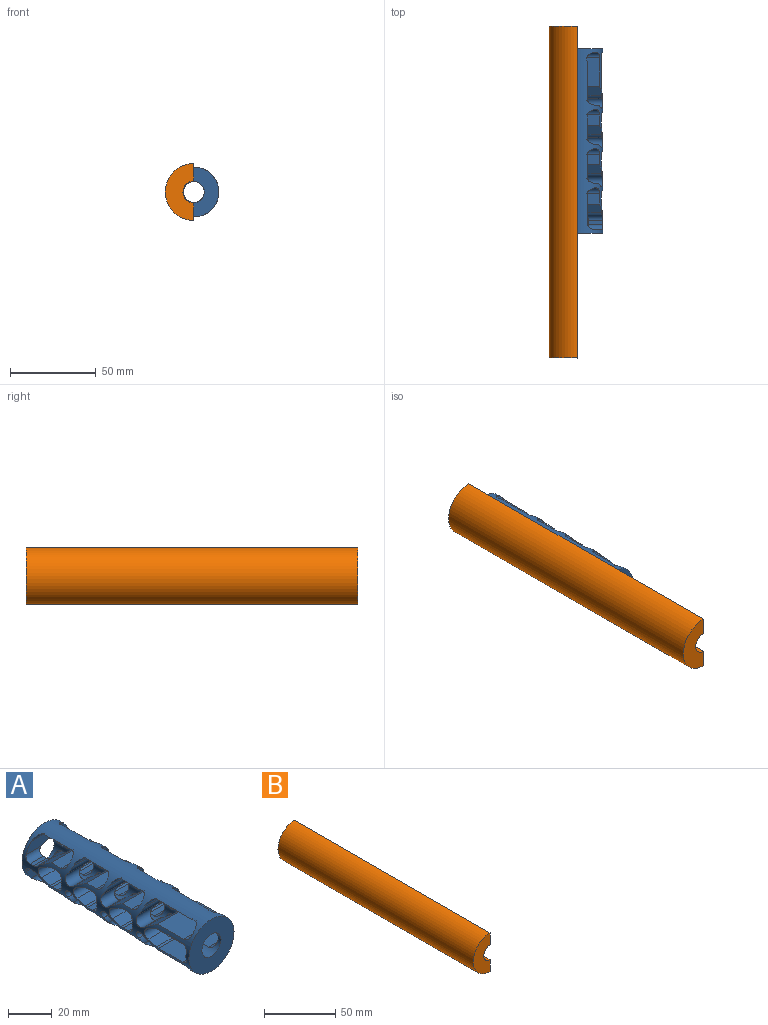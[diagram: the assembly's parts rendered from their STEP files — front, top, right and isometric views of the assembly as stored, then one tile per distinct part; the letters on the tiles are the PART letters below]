
ASSEMBLY  parts=2 mates=1
PART A: 185 faces, bbox 29.1x107.6x29.1 mm
  f0: plane 8.74x4.19mm, normal (0,1,0), area 35.3mm2, adj f57,f61,f183,f184
  f1: plane 15.44x10.34mm, normal (0,0,1), area 159.6mm2, adj f3,f57,f61,f184
  f2: plane 15.44x10.34mm, normal (0,0,1), area 159.6mm2, adj f61,f65,f180,f184
  f3: cylinder r=3.17mm len=10.43mm, axis (1,0,0), area 12.9mm2, adj f1,f4,f61,f184
  f4: plane 10.65x4.96mm, normal (0,-0.39,0.92), area 50.1mm2, adj f3,f5,f61,f184
  f5: cylinder r=3.2mm len=9.12mm, axis (1,0,0), area 63.7mm2, adj f4,f6,f61,f184
  f6: plane 10.67x4.96mm, normal (0,-0.39,-0.92), area 50.2mm2, adj f5,f7,f61,f184
  f7: cylinder r=3.17mm len=10.46mm, axis (1,0,0), area 13mm2, adj f6,f8,f61,f184
  f8: plane 15.39x10.36mm, normal (0,0,-1), area 159.5mm2, adj f7,f61,f183,f184
  f9: plane 15.39x10.36mm, normal (0,0,-1), area 159.5mm2, adj f58,f61,f69,f184
  f10: cylinder r=4.43mm len=9.66mm, axis (1,0,0), area 20.6mm2, adj f61,f73,f75,f184
  f11: plane 25.34x16.92mm, normal (0,0,-1), area 428.7mm2, adj f61,f75,f181
  f12: plane 25.34x16.92mm, normal (0,0,1), area 428.7mm2, adj f61,f80,f182
  f13: cylinder r=4.43mm len=9.66mm, axis (1,0,0), area 20.5mm2, adj f61,f80,f82,f184
  f14: plane 10.34x3.44mm, normal (0,0,1), area 35.5mm2, adj f15,f23,f61,f184
  f15: cylinder r=3.17mm len=10.43mm, axis (1,0,0), area 12.9mm2, adj f14,f16,f61,f184
  f16: plane 10.65x4.96mm, normal (0,-0.39,0.92), area 50.1mm2, adj f15,f17,f61,f184
  f17: cylinder r=3.2mm len=9.12mm, axis (1,0,0), area 63.7mm2, adj f16,f18,f61,f184
  f18: plane 10.67x4.96mm, normal (0,-0.39,-0.92), area 50.2mm2, adj f17,f19,f61,f184
  f19: cylinder r=3.17mm len=10.46mm, axis (1,0,0), area 13mm2, adj f18,f20,f61,f184
  f20: plane 10.36x3.38mm, normal (0,0,-1), area 35mm2, adj f19,f21,f61,f184
  f21: cylinder r=3.17mm len=11.05mm, axis (1,0,0), area 39.6mm2, adj f20,f22,f61,f184
  f22: cylinder r=10.73mm len=9.15mm, axis (1,0,0), area 51.3mm2, adj f21,f23,f61,f184
  f23: cylinder r=3.17mm len=11.02mm, axis (1,0,0), area 39.6mm2, adj f14,f22,f61,f184
  f24: cylinder r=4.43mm len=9.66mm, axis (1,0,0), area 20.6mm2, adj f61,f98,f100,f184
  f25: cylinder r=4.43mm len=9.66mm, axis (1,0,0), area 20.5mm2, adj f61,f109,f111,f184
  f26: plane 10.34x3.44mm, normal (0,0,1), area 35.5mm2, adj f27,f35,f61,f184
  f27: cylinder r=3.17mm len=10.43mm, axis (1,0,0), area 12.9mm2, adj f26,f28,f61,f184
  f28: plane 10.65x4.96mm, normal (0,-0.39,0.92), area 50.1mm2, adj f27,f29,f61,f184
  f29: cylinder r=3.2mm len=9.12mm, axis (1,0,0), area 63.7mm2, adj f28,f30,f61,f184
  f30: plane 10.67x4.96mm, normal (0,-0.39,-0.92), area 50.2mm2, adj f29,f31,f61,f184
  f31: cylinder r=3.17mm len=10.46mm, axis (1,0,0), area 13mm2, adj f30,f32,f61,f184
  f32: plane 10.36x3.38mm, normal (0,0,-1), area 35mm2, adj f31,f33,f61,f184
  f33: cylinder r=3.17mm len=11.05mm, axis (1,0,0), area 39.6mm2, adj f32,f34,f61,f184
  f34: cylinder r=10.73mm len=9.15mm, axis (1,0,0), area 51.3mm2, adj f33,f35,f61,f184
  f35: cylinder r=3.17mm len=11.02mm, axis (1,0,0), area 39.6mm2, adj f26,f34,f61,f184
  f36: cylinder r=4.43mm len=9.66mm, axis (1,0,0), area 20.6mm2, adj f61,f127,f129,f184
  f37: cylinder r=4.43mm len=9.66mm, axis (1,0,0), area 20.5mm2, adj f61,f138,f140,f184
  f38: plane 10.34x3.44mm, normal (0,0,1), area 35.5mm2, adj f39,f47,f61,f184
  f39: cylinder r=3.17mm len=10.43mm, axis (1,0,0), area 12.9mm2, adj f38,f40,f61,f184
  f40: plane 10.65x4.96mm, normal (0,-0.39,0.92), area 50.1mm2, adj f39,f41,f61,f184
  f41: cylinder r=3.2mm len=9.12mm, axis (1,0,0), area 63.7mm2, adj f40,f42,f61,f184
  f42: plane 10.67x4.96mm, normal (0,-0.39,-0.92), area 50.2mm2, adj f41,f43,f61,f184
  f43: cylinder r=3.17mm len=10.46mm, axis (1,0,0), area 13mm2, adj f42,f44,f61,f184
  f44: plane 10.36x3.38mm, normal (0,0,-1), area 35mm2, adj f43,f45,f61,f184
  f45: cylinder r=3.17mm len=11.05mm, axis (1,0,0), area 39.6mm2, adj f44,f46,f61,f184
  f46: cylinder r=10.73mm len=9.15mm, axis (1,0,0), area 51.3mm2, adj f45,f47,f61,f184
  f47: cylinder r=3.17mm len=11.02mm, axis (1,0,0), area 39.6mm2, adj f38,f46,f61,f184
  f48: cylinder r=3.17mm len=8.92mm, axis (1,0,0), area 24.6mm2, adj f49,f56,f61,f184
  f49: cylinder r=4.43mm len=9.66mm, axis (1,0,0), area 20.6mm2, adj f48,f61,f155,f184
  f50: cylinder r=4.43mm len=9.66mm, axis (1,0,0), area 20.5mm2, adj f51,f61,f162,f184
  f51: cylinder r=3.17mm len=8.92mm, axis (1,0,0), area 24.6mm2, adj f50,f53,f61,f184
  f52: cylinder r=3.17mm len=10.43mm, axis (1,0,0), area 43.9mm2, adj f53,f61,f172,f184
  f53: plane 8.48x2.48mm, normal (0,0,1), area 21.1mm2, adj f51,f52,f61,f184
  f54: cylinder r=3.17mm len=10.4mm, axis (1,0,0), area 43.9mm2, adj f55,f61,f176,f184
  f55: plane 8.47x2.48mm, normal (0,0,-1), area 21mm2, adj f54,f56,f61,f184
  f56: plane 8.48x0.03mm, normal (0,1,0), area 0.2mm2, adj f48,f55,f61,f184
  f57: cylinder r=3.17mm len=11.17mm, axis (1,0,0), area 47.3mm2, adj f0,f1,f61,f184
  f58: cylinder r=3.17mm len=11.2mm, axis (-1,0,0), area 47.4mm2, adj f9,f60,f61,f184
  f59: plane 20.52x0.06mm, normal (0,1,0), area 1.1mm2, adj f61,f165,f181
  f60: plane 8.74x4.19mm, normal (0,1,0), area 35.3mm2, adj f58,f61,f180,f184
  f61: cylinder r=14.53mm len=107.57mm, axis (0,1,0), area 4158.4mm2, adj f0,f1,f2,f3,f4,f5,f6,f7
  f62: cylinder r=3.18mm len=10.94mm, axis (1,0,0), area 6.7mm2, adj f61,f76,f166
  f63: plane 29.06x29.06mm, normal (0,-1,0), area 544mm2, adj f61,f184
  f64: plane 29.06x29.06mm, normal (0,1,0), area 544mm2, adj f61,f184
  f65: cylinder r=3.17mm len=10.43mm, axis (1,0,0), area 12.9mm2, adj f2,f61,f66,f184
  f66: plane 10.65x4.96mm, normal (0,-0.39,0.92), area 50.1mm2, adj f61,f65,f67,f184
  f67: cylinder r=3.2mm len=9.12mm, axis (1,0,0), area 63.7mm2, adj f61,f66,f68,f184
  f68: plane 10.67x4.96mm, normal (0,-0.39,-0.92), area 50.2mm2, adj f61,f67,f69,f184
  f69: cylinder r=3.17mm len=10.46mm, axis (1,0,0), area 13mm2, adj f9,f61,f68,f184
  f70: cylinder r=3.17mm len=20.9mm, axis (1,0,0), area 73.1mm2, adj f61,f71,f76
  f71: cylinder r=5.04mm len=25.84mm, axis (1,0,0), area 87.1mm2, adj f61,f70,f72
  f72: cylinder r=10.78mm len=25.88mm, axis (1,0,0), area 1.4mm2, adj f61,f71,f73
  f73: cylinder r=3.17mm len=28.91mm, axis (1,0,0), area 184.8mm2, adj f10,f61,f72,f74,f184
  f74: cylinder r=4.43mm len=9.66mm, axis (1,0,0), area 20.6mm2, adj f61,f73,f75,f184
  f75: plane 27.89x5.13mm, normal (0,0.51,-0.86), area 133.2mm2, adj f10,f11,f61,f74,f184
  f76: plane 22.91x10.94mm, normal (0,0,1), area 250.5mm2, adj f61,f62,f70
  f77: cylinder r=5.04mm len=25.83mm, axis (1,0,0), area 87mm2, adj f61,f78,f84
  f78: cylinder r=3.17mm len=20.9mm, axis (1,0,0), area 73.1mm2, adj f61,f77,f79
  f79: plane 22.88x10.94mm, normal (0,0,-1), area 250.3mm2, adj f61,f78,f167
  f80: plane 27.89x5.13mm, normal (0,0.51,0.86), area 133.3mm2, adj f12,f13,f61,f81,f184
  f81: cylinder r=4.43mm len=9.66mm, axis (1,0,0), area 20.5mm2, adj f61,f80,f82,f184
  f82: cylinder r=3.17mm len=28.91mm, axis (1,0,0), area 184.8mm2, adj f13,f61,f81,f83,f184
  f83: cylinder r=10.78mm len=25.88mm, axis (1,0,0), area 1.4mm2, adj f61,f82,f84
  f84: plane 25.84x0mm, normal (0,-0.79,-0.62), area 0.1mm2, adj f61,f77,f83
  f85: plane 10.34x3.44mm, normal (0,0,1), area 35.5mm2, adj f61,f86,f94,f184
  f86: cylinder r=3.17mm len=10.43mm, axis (1,0,0), area 12.9mm2, adj f61,f85,f87,f184
  f87: plane 10.65x4.96mm, normal (0,-0.39,0.92), area 50.1mm2, adj f61,f86,f88,f184
  f88: cylinder r=3.2mm len=9.12mm, axis (1,0,0), area 63.7mm2, adj f61,f87,f89,f184
  f89: plane 10.67x4.96mm, normal (0,-0.39,-0.92), area 50.2mm2, adj f61,f88,f90,f184
  f90: cylinder r=3.17mm len=10.46mm, axis (1,0,0), area 13mm2, adj f61,f89,f91,f184
  f91: plane 10.36x3.38mm, normal (0,0,-1), area 35mm2, adj f61,f90,f92,f184
  f92: cylinder r=3.17mm len=11.05mm, axis (1,0,0), area 39.6mm2, adj f61,f91,f93,f184
  f93: cylinder r=10.73mm len=9.15mm, axis (1,0,0), area 51.3mm2, adj f61,f92,f94,f184
  f94: cylinder r=3.17mm len=11.02mm, axis (1,0,0), area 39.6mm2, adj f61,f85,f93,f184
  f95: cylinder r=3.17mm len=20.9mm, axis (1,0,0), area 73.1mm2, adj f61,f96,f103
  f96: cylinder r=5.04mm len=25.84mm, axis (1,0,0), area 87.1mm2, adj f61,f95,f97
  f97: cylinder r=10.78mm len=25.88mm, axis (1,0,0), area 1.4mm2, adj f61,f96,f98
  f98: cylinder r=3.17mm len=28.91mm, axis (1,0,0), area 184.8mm2, adj f24,f61,f97,f99,f184
  f99: cylinder r=4.43mm len=9.66mm, axis (1,0,0), area 20.6mm2, adj f61,f98,f100,f184
  f100: plane 27.89x5.13mm, normal (0,0.51,-0.86), area 133.2mm2, adj f24,f61,f99,f101,f184
  f101: plane 25.34x6.28mm, normal (0,0,-1), area 159.2mm2, adj f61,f100,f102
  f102: cylinder r=3.18mm len=25.34mm, axis (1,0,0), area 193.1mm2, adj f61,f101,f103
  f103: plane 14.54x10.94mm, normal (0,0,1), area 159mm2, adj f61,f95,f102
  f104: cylinder r=5.04mm len=25.83mm, axis (1,0,0), area 87mm2, adj f61,f105,f113
  f105: cylinder r=3.17mm len=20.9mm, axis (1,0,0), area 73.1mm2, adj f61,f104,f106
  f106: plane 14.54x10.94mm, normal (0,0,-1), area 159mm2, adj f61,f105,f107
  f107: cylinder r=3.17mm len=25.34mm, axis (1,0,0), area 193.4mm2, adj f61,f106,f108
  f108: plane 25.34x6.28mm, normal (0,0,1), area 159.2mm2, adj f61,f107,f109
  f109: plane 27.89x5.13mm, normal (0,0.51,0.86), area 133.3mm2, adj f25,f61,f108,f110,f184
  f110: cylinder r=4.43mm len=9.66mm, axis (1,0,0), area 20.5mm2, adj f61,f109,f111,f184
  f111: cylinder r=3.17mm len=28.91mm, axis (1,0,0), area 184.8mm2, adj f25,f61,f110,f112,f184
  f112: cylinder r=10.78mm len=25.88mm, axis (1,0,0), area 1.4mm2, adj f61,f111,f113
  f113: plane 25.84x0mm, normal (0,-0.79,-0.62), area 0.1mm2, adj f61,f104,f112
  f114: plane 10.34x3.44mm, normal (0,0,1), area 35.5mm2, adj f61,f115,f123,f184
  f115: cylinder r=3.17mm len=10.43mm, axis (1,0,0), area 12.9mm2, adj f61,f114,f116,f184
  f116: plane 10.65x4.96mm, normal (0,-0.39,0.92), area 50.1mm2, adj f61,f115,f117,f184
  f117: cylinder r=3.2mm len=9.12mm, axis (1,0,0), area 63.7mm2, adj f61,f116,f118,f184
  f118: plane 10.67x4.96mm, normal (0,-0.39,-0.92), area 50.2mm2, adj f61,f117,f119,f184
  f119: cylinder r=3.17mm len=10.46mm, axis (1,0,0), area 13mm2, adj f61,f118,f120,f184
  f120: plane 10.36x3.38mm, normal (0,0,-1), area 35mm2, adj f61,f119,f121,f184
  f121: cylinder r=3.17mm len=11.05mm, axis (1,0,0), area 39.6mm2, adj f61,f120,f122,f184
  f122: cylinder r=10.73mm len=9.15mm, axis (1,0,0), area 51.3mm2, adj f61,f121,f123,f184
  f123: cylinder r=3.17mm len=11.02mm, axis (1,0,0), area 39.6mm2, adj f61,f114,f122,f184
  f124: cylinder r=3.17mm len=20.9mm, axis (1,0,0), area 73.1mm2, adj f61,f125,f132
  f125: cylinder r=5.04mm len=25.84mm, axis (1,0,0), area 87.1mm2, adj f61,f124,f126
  f126: cylinder r=10.78mm len=25.88mm, axis (1,0,0), area 1.4mm2, adj f61,f125,f127
  f127: cylinder r=3.17mm len=28.91mm, axis (1,0,0), area 184.8mm2, adj f36,f61,f126,f128,f184
  f128: cylinder r=4.43mm len=9.66mm, axis (1,0,0), area 20.6mm2, adj f61,f127,f129,f184
  f129: plane 27.89x5.13mm, normal (0,0.51,-0.86), area 133.2mm2, adj f36,f61,f128,f130,f184
  f130: plane 25.34x6.28mm, normal (0,0,-1), area 159.2mm2, adj f61,f129,f131
  f131: cylinder r=3.18mm len=25.34mm, axis (1,0,0), area 193.1mm2, adj f61,f130,f132
  f132: plane 14.54x10.94mm, normal (0,0,1), area 159mm2, adj f61,f124,f131
  f133: cylinder r=5.04mm len=25.83mm, axis (1,0,0), area 87mm2, adj f61,f134,f142
  f134: cylinder r=3.17mm len=20.9mm, axis (1,0,0), area 73.1mm2, adj f61,f133,f135
  f135: plane 14.54x10.94mm, normal (0,0,-1), area 159mm2, adj f61,f134,f136
  f136: cylinder r=3.17mm len=25.34mm, axis (1,0,0), area 193.4mm2, adj f61,f135,f137
  f137: plane 25.34x6.28mm, normal (0,0,1), area 159.2mm2, adj f61,f136,f138
  f138: plane 27.89x5.13mm, normal (0,0.51,0.86), area 133.3mm2, adj f37,f61,f137,f139,f184
  f139: cylinder r=4.43mm len=9.66mm, axis (1,0,0), area 20.5mm2, adj f61,f138,f140,f184
  f140: cylinder r=3.17mm len=28.91mm, axis (1,0,0), area 184.8mm2, adj f37,f61,f139,f141,f184
  f141: cylinder r=10.78mm len=25.88mm, axis (1,0,0), area 1.4mm2, adj f61,f140,f142
  f142: plane 25.84x0mm, normal (0,-0.79,-0.62), area 0.1mm2, adj f61,f133,f141
  f143: plane 10.34x3.44mm, normal (0,0,1), area 35.5mm2, adj f61,f144,f152,f184
  f144: cylinder r=3.17mm len=10.43mm, axis (1,0,0), area 12.9mm2, adj f61,f143,f145,f184
  f145: plane 10.65x4.96mm, normal (0,-0.39,0.92), area 50.1mm2, adj f61,f144,f146,f184
  f146: cylinder r=3.2mm len=9.12mm, axis (1,0,0), area 63.7mm2, adj f61,f145,f147,f184
  f147: plane 10.67x4.96mm, normal (0,-0.39,-0.92), area 50.2mm2, adj f61,f146,f148,f184
  f148: cylinder r=3.17mm len=10.46mm, axis (1,0,0), area 13mm2, adj f61,f147,f149,f184
  f149: plane 10.36x3.38mm, normal (0,0,-1), area 35mm2, adj f61,f148,f150,f184
  f150: cylinder r=3.17mm len=11.05mm, axis (1,0,0), area 39.6mm2, adj f61,f149,f151,f184
  f151: cylinder r=10.73mm len=9.15mm, axis (1,0,0), area 51.3mm2, adj f61,f150,f152,f184
  f152: cylinder r=3.17mm len=11.02mm, axis (1,0,0), area 39.6mm2, adj f61,f143,f151,f184
  f153: cylinder r=3.17mm len=8.92mm, axis (1,0,0), area 24.6mm2, adj f61,f154,f179,f184
  f154: cylinder r=4.43mm len=9.66mm, axis (1,0,0), area 20.6mm2, adj f61,f153,f155,f184
  f155: plane 27.89x5.13mm, normal (0,0.51,-0.86), area 133.2mm2, adj f49,f61,f154,f156,f184
  f156: plane 25.34x6.28mm, normal (0,0,-1), area 159.2mm2, adj f61,f155,f157
  f157: cylinder r=3.18mm len=25.34mm, axis (1,0,0), area 193.1mm2, adj f61,f156,f158
  f158: plane 18.19x10.94mm, normal (0,0,1), area 199mm2, adj f61,f157,f175
  f159: plane 18.19x10.94mm, normal (0,0,-1), area 199mm2, adj f61,f160,f173
  f160: cylinder r=3.17mm len=25.34mm, axis (1,0,0), area 193.4mm2, adj f61,f159,f161
  f161: plane 25.34x6.28mm, normal (0,0,1), area 159.2mm2, adj f61,f160,f162
  f162: plane 27.89x5.13mm, normal (0,0.51,0.86), area 133.3mm2, adj f50,f61,f161,f163,f184
  f163: cylinder r=4.43mm len=9.66mm, axis (1,0,0), area 20.5mm2, adj f61,f162,f164,f184
  f164: cylinder r=3.17mm len=8.92mm, axis (1,0,0), area 24.6mm2, adj f61,f163,f174,f184
  f165: cylinder r=3.17mm len=20.41mm, axis (1,0,0), area 73.9mm2, adj f59,f61,f166
  f166: plane 10.66x1.65mm, normal (0,0,1), area 17.6mm2, adj f61,f62,f165
  f167: cylinder r=3.18mm len=10.94mm, axis (1,0,0), area 6.7mm2, adj f61,f79,f168
  f168: plane 10.66x1.68mm, normal (0,0,-1), area 17.9mm2, adj f61,f167,f169
  f169: cylinder r=3.17mm len=20.41mm, axis (1,0,0), area 73.9mm2, adj f61,f168,f170
  f170: plane 20.52x0.06mm, normal (0,1,0), area 1.1mm2, adj f61,f169,f182
  f171: cylinder r=3.17mm len=10.43mm, axis (1,0,0), area 43.9mm2, adj f61,f172,f174,f184
  f172: plane 27.52x5.62mm, normal (0,-1,0), area 130.2mm2, adj f52,f61,f171,f173,f184
  f173: cylinder r=3.17mm len=20.52mm, axis (1,0,0), area 74.9mm2, adj f61,f159,f172
  f174: plane 8.48x2.48mm, normal (0,0,1), area 21.1mm2, adj f61,f164,f171,f184
  f175: cylinder r=3.17mm len=20.52mm, axis (1,0,0), area 74.9mm2, adj f61,f158,f176
  f176: plane 27.54x5.65mm, normal (0,-1,0), area 130.7mm2, adj f54,f61,f175,f177,f184
  f177: cylinder r=3.17mm len=10.4mm, axis (1,0,0), area 43.9mm2, adj f61,f176,f178,f184
  f178: plane 8.47x2.48mm, normal (0,0,-1), area 21mm2, adj f61,f177,f179,f184
  f179: plane 8.48x0.03mm, normal (0,1,0), area 0.2mm2, adj f61,f153,f178,f184
  f180: cylinder r=3.17mm len=11.17mm, axis (1,0,0), area 47.3mm2, adj f2,f60,f61,f184
  f181: cylinder r=3.17mm len=25.34mm, axis (1,0,0), area 118.6mm2, adj f11,f59,f61
  f182: cylinder r=3.17mm len=25.34mm, axis (1,0,0), area 118.6mm2, adj f12,f61,f170
  f183: cylinder r=3.17mm len=11.2mm, axis (-1,0,0), area 47.4mm2, adj f0,f8,f61,f184
  f184: cylinder r=6.16mm len=107.57mm, axis (0,-1,0), area 1581.8mm2, adj f0,f1,f2,f3,f4,f5,f6,f7
PART B: 10 faces, bbox 16.6x193.7x33.3 mm
  f0: plane 193.68x10.29mm, normal (1,0,0), area 593.9mm2, adj f1,f2,f3,f4,f6,f7,f8,f9
  f1: cylinder r=14.55mm len=170.46mm, axis (0,1,0), area 7794mm2, adj f0,f5,f6,f7
  f2: cylinder r=16.64mm len=193.68mm, axis (0,1,0), area 10122.7mm2, adj f0,f3,f4,f5
  f3: plane 33.27x16.64mm, normal (0,-1,0), area 371.4mm2, adj f0,f2,f5,f9
  f4: plane 33.27x16.64mm, normal (0,1,0), area 371.4mm2, adj f0,f2,f5,f8
  f5: plane 193.68x10.29mm, normal (1,0,0), area 593.9mm2, adj f1,f2,f3,f4,f6,f7,f8,f9
  f6: plane 29.11x14.55mm, normal (0,1,0), area 269.4mm2, adj f0,f1,f5,f9
  f7: plane 29.11x14.55mm, normal (0,-1,0), area 269.4mm2, adj f0,f1,f5,f8
  f8: cylinder r=6.35mm len=13.06mm, axis (0,-1,0), area 260.4mm2, adj f0,f4,f5,f7
  f9: cylinder r=6.35mm len=12.7mm, axis (0,-1,0), area 202.7mm2, adj f0,f3,f5,f6
PLACE A rot(axis=(1,0,0),180deg) t=(-37.57,-69.37,-28.27)mm
PLACE B t=(-37.57,51.5,-28.27)mm fixed
MATE cylindrical A.f61 <-> B.f1  axis (0,-1,0) through (-37.57,-15.58,-28.27)mm
